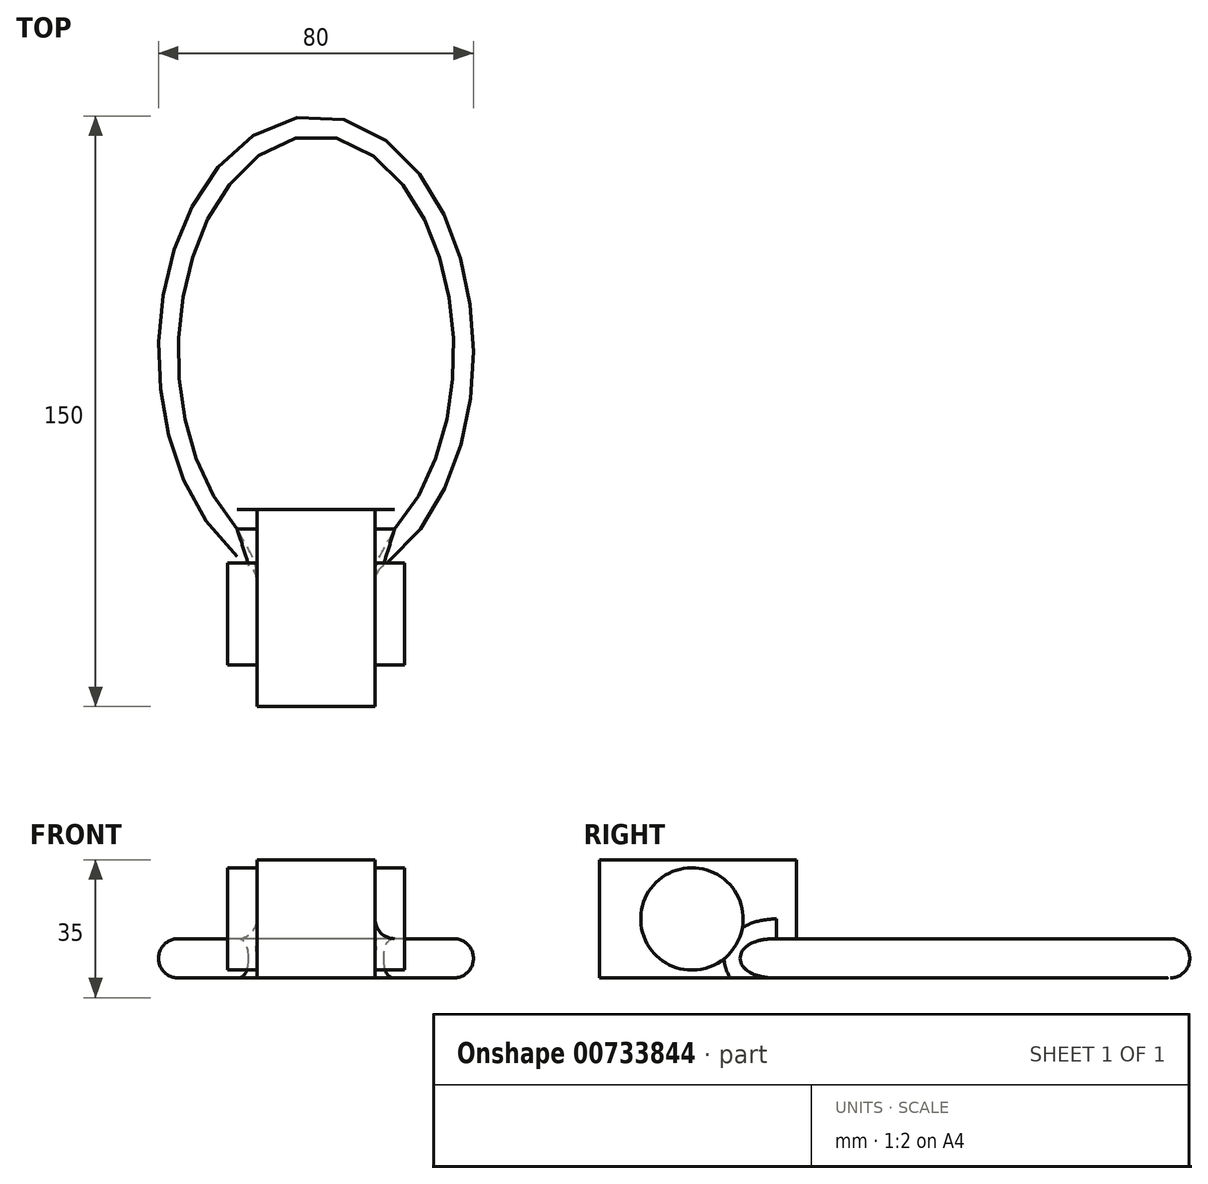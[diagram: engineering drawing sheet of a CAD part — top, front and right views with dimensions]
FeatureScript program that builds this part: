
annotation { "Feature Type Name" : "Feature", "Feature Type Description" : "" }
export const myFeature = defineFeature(function(context is Context, id is Id, definition is map)
    precondition{}
    {
        {
            var Q0;
            Q0=qCreatedBy(makeId("Top.planeOp"),FACE);
            var sketch = newSketch(context, id + "F0", { "sketchPlane" : qUnion([Q0])});
            skEllipse(sketch, "E0", {"center": v(0, 0) * mm, "majorRadius": 60 * mm, "minorRadius": 40 * mm, "majorAxis": v(0, -1)});
            skPoint(sketch, "E1", {"position": v(0, -98.1) * mm});
            skLineSegment(sketch, "E2", {"start": v(0, -98.1) * mm, "end": v(-10, -98.1) * mm});
            skLineSegment(sketch, "E3", {"start": v(0, -98.1) * mm, "end": v(10, -98.1) * mm});
            skLineSegment(sketch, "E4", {"start": v(-10, -98.1) * mm, "end": v(-10, -58.1) * mm});
            skLineSegment(sketch, "E5", {"start": v(10, -98.1) * mm, "end": v(10, -58.1) * mm});
            skPoint(sketch, "E6", {"position": v(0, 60) * mm});
            skSolve(sketch);
        }
        {
            var Q0;
            {var subQ0=sQuery(id+"F0.wireOp",EDGE,"E0");var subQ1=makeQuery(id+"F0.imprint","INTERSECT",VERTEX,{"derivedFrom":[subQ0,sQuery(id+"F0.wireOp",EDGE,"E4")]});Q0=makeQuery(id+"F0.imprint","IMPRINT",FACE,{"disambiguationData":[TD([[makeQuery(id+"F0.imprint","IMPRINT",EDGE,{"disambiguationData":[TD([[subQ1,1.0]])],"derivedFrom":subQ0}),1.0]])]});}
            extrude(context, id + "F1", {"entities" : qUnion([Q0]), "depth" : 10 * mm, "offsetDistance" : 25 * mm});
        }
        {
            var Q0;
            Q0=qCreatedBy(makeId("Top.planeOp"),FACE);
            cPlane(context, id + "F2", {"entities" : qUnion([Q0]), "cplaneType" : CPlaneType.OFFSET, "offset" : 15 * mm, "width" : 150 * mm, "height" : 150 * mm});
        }
        {
            var Q0;
            Q0=qCreatedBy(id+"F2.planeOp",FACE);
            var sketch = newSketch(context, id + "F3", { "sketchPlane" : qUnion([Q0])});
            skPoint(sketch, "E7", {"position": v(0, 0) * mm});
            skLineSegment(sketch, "E8", {"start": v(0, 0) * mm, "end": v(0, -90) * mm});
            skLineSegment(sketch, "E9.bottom", {"start": v(-15, -90) * mm, "end": v(15, -90) * mm});
            skLineSegment(sketch, "E9.top", {"start": v(-15, -40) * mm, "end": v(15, -40) * mm});
            skLineSegment(sketch, "E9.left", {"start": v(-15, -90) * mm, "end": v(-15, -40) * mm});
            skLineSegment(sketch, "E9.right", {"start": v(15, -90) * mm, "end": v(15, -40) * mm});
            skPoint(sketch, "E9.middle", {"position": v(0, -65) * mm});
            skPoint(sketch, "E10", {"position": v(0, -45) * mm});
            skSolve(sketch);
        }
        {
            var Q0;
            {var subQ5=sQuery(id+"F3.wireOp",EDGE,"E9.right");Q0=makeQuery(id+"F3.imprint","IMPRINT",FACE,{"disambiguationData":[TD([[makeQuery(id+"F3.imprint","IMPRINT",EDGE,{"derivedFrom":subQ5}),1.0]])]});}
            var Q1;
            {var subQ5=sQuery(id+"F3.wireOp",EDGE,"E9.left");Q1=makeQuery(id+"F3.imprint","IMPRINT",FACE,{"disambiguationData":[TD([[makeQuery(id+"F3.imprint","IMPRINT",EDGE,{"derivedFrom":subQ5}),-1.0]])]});}
            extrude(context, id + "F4", {"entities" : qUnion([Q0, Q1]), "operationType" : NewBodyOperationType.ADD, "endBound" : BoundingType.SYMMETRIC, "depth" : 30 * mm, "offsetDistance" : 25 * mm});
        }
        {
            var Q0;
            Q0=makeQuery(id+"F1.opExtrude","CAP_EDGE",EDGE,{"disambiguationData":[OSD([sQuery(id+"F0.wireOp",EDGE,"E0")])],"isStart":true});
            var Q1;
            Q1=makeQuery(id+"F1.opExtrude","CAP_EDGE",EDGE,{"disambiguationData":[OSD([sQuery(id+"F0.wireOp",EDGE,"E0")])],"isStart":false});
            fillet(context, id + "F5", {"entities" : qUnion([Q0, Q1]), "radius" : 5 * mm, "tangentPropagation" : true, "allowEdgeOverflow" : false});
        }
        {
            var Q0;
            Q0=qCreatedBy(makeId("Right.planeOp"),FACE);
            var sketch = newSketch(context, id + "F6", { "sketchPlane" : qUnion([Q0])});
            skPoint(sketch, "E11", {"position": v(0, 15) * mm});
            skPoint(sketch, "E12", {"position": v(-66.5, 15) * mm});
            skCircle(sketch, "E13", {"center": v(-66.5, 15) * mm, "radius": 13 * mm});
            skSolve(sketch);
        }
        {
            var Q0;
            Q0 = qSketchRegion(id + "F6", true);
            extrude(context, id + "F7", {"entities" : qUnion([Q0]), "operationType" : NewBodyOperationType.ADD, "endBound" : BoundingType.SYMMETRIC, "depth" : 45 * mm, "offsetDistance" : 25 * mm});
        }
        {
            var Q0;
            Q0=makeQuery(id+"F5.opFillet","BLEND_EDGE",EDGE,{"blendedFrom":[makeQuery(id+"F1.opExtrude","CAP_EDGE",EDGE,{"disambiguationData":[OSD([sQuery(id+"F0.wireOp",EDGE,"E0")])],"isStart":false}),makeQuery(id+"F4.opExtrude","SWEPT_FACE",FACE,{"disambiguationData":[OSD([sQuery(id+"F3.wireOp",EDGE,"E9.left")])]})],"blendedInto":[makeQuery(id+"F4.opExtrude","SWEPT_FACE",FACE,{"disambiguationData":[OSD([sQuery(id+"F3.wireOp",EDGE,"E9.left")])]})]});
            var Q1;
            Q1=makeQuery(id+"F5.opFillet","BLEND_EDGE",EDGE,{"blendedFrom":[makeQuery(id+"F1.opExtrude","CAP_EDGE",EDGE,{"disambiguationData":[OSD([sQuery(id+"F0.wireOp",EDGE,"E0")])],"isStart":true}),makeQuery(id+"F4.opExtrude","SWEPT_FACE",FACE,{"disambiguationData":[OSD([sQuery(id+"F3.wireOp",EDGE,"E9.left")])]})],"blendedInto":[makeQuery(id+"F4.opExtrude","SWEPT_FACE",FACE,{"disambiguationData":[OSD([sQuery(id+"F3.wireOp",EDGE,"E9.left")])]})]});
            var Q2;
            Q2=makeQuery(id+"F5.opFillet","BLEND_EDGE",EDGE,{"blendedFrom":[makeQuery(id+"F1.opExtrude","CAP_EDGE",EDGE,{"disambiguationData":[OSD([sQuery(id+"F0.wireOp",EDGE,"E0")])],"isStart":false}),makeQuery(id+"F4.opExtrude","SWEPT_FACE",FACE,{"disambiguationData":[OSD([sQuery(id+"F3.wireOp",EDGE,"E9.right")])]})],"blendedInto":[makeQuery(id+"F4.opExtrude","SWEPT_FACE",FACE,{"disambiguationData":[OSD([sQuery(id+"F3.wireOp",EDGE,"E9.right")])]})]});
            var Q3;
            Q3=makeQuery(id+"F5.opFillet","BLEND_EDGE",EDGE,{"blendedFrom":[makeQuery(id+"F1.opExtrude","CAP_EDGE",EDGE,{"disambiguationData":[OSD([sQuery(id+"F0.wireOp",EDGE,"E0")])],"isStart":true}),makeQuery(id+"F4.opExtrude","SWEPT_FACE",FACE,{"disambiguationData":[OSD([sQuery(id+"F3.wireOp",EDGE,"E9.right")])]})],"blendedInto":[makeQuery(id+"F4.opExtrude","SWEPT_FACE",FACE,{"disambiguationData":[OSD([sQuery(id+"F3.wireOp",EDGE,"E9.right")])]})]});
            fillet(context, id + "F8", {"entities" : qUnion([Q0, Q1, Q2, Q3]), "radius" : 5 * mm, "tangentPropagation" : true, "allowEdgeOverflow" : false});
        }
    });
